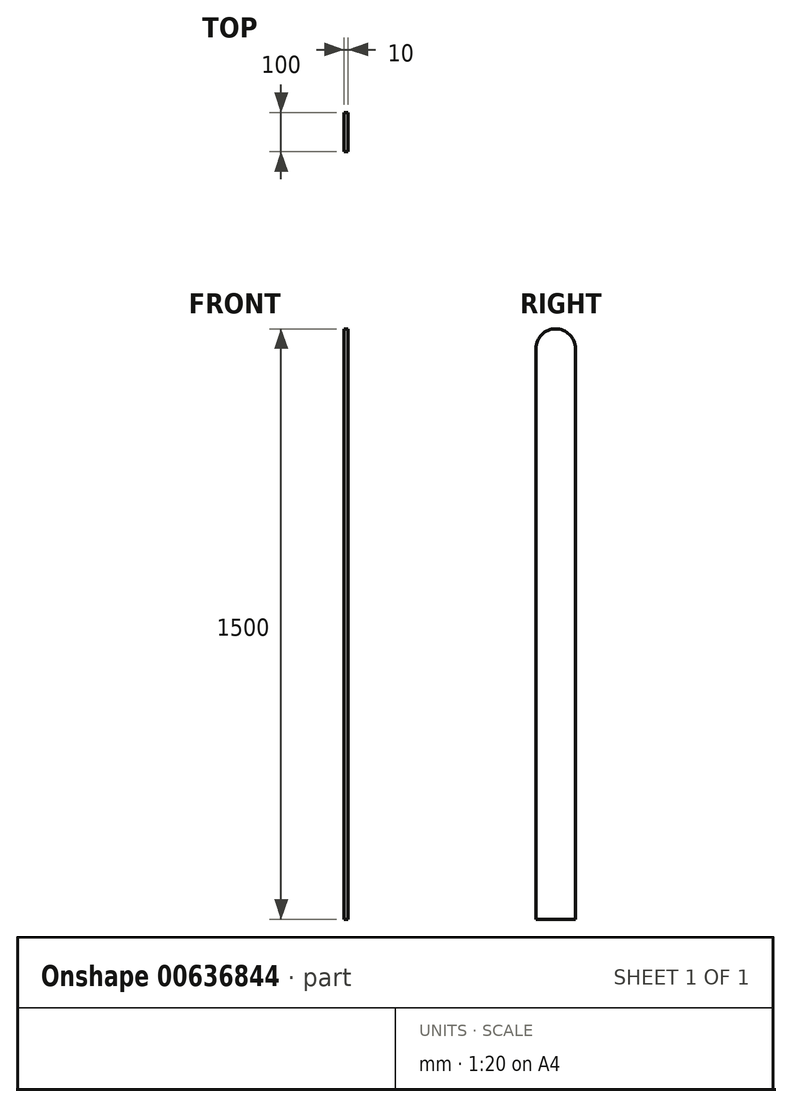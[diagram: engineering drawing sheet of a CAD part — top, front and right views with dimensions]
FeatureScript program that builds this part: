
annotation { "Feature Type Name" : "Feature", "Feature Type Description" : "" }
export const myFeature = defineFeature(function(context is Context, id is Id, definition is map)
    precondition{}
    {
        {
            var Q0;
            Q0=qCreatedBy(makeId("Right.planeOp"),FACE);
            var sketch = newSketch(context, id + "F0", { "sketchPlane" : qUnion([Q0])});
            skLineSegment(sketch, "E0.bottom", {"start": v(0, 0) * mm, "end": v(100, 0) * mm});
            skLineSegment(sketch, "E0.left", {"start": v(0, 0) * mm, "end": v(0, 1450) * mm});
            skLineSegment(sketch, "E0.right", {"start": v(100, 0) * mm, "end": v(100, 1450) * mm});
            skArc(sketch, "E1", {"start": v(100, 1450) * mm, "mid": v(50, 1500) * mm, "end": v(0, 1450) * mm});
            skSolve(sketch);
        }
        {
            var Q0;
            Q0=makeQuery(id+"F0.imprint","IMPRINT",FACE,{"disambiguationData":[TD([[makeQuery(id+"F0.imprint","IMPRINT",EDGE,{"derivedFrom":sQuery(id+"F0.wireOp",EDGE,"E0.bottom")}),1.0]])]});
            extrude(context, id + "F1", {"entities" : qUnion([Q0]), "depth" : 10 * mm, "offsetDistance" : 25 * mm});
        }
    });
